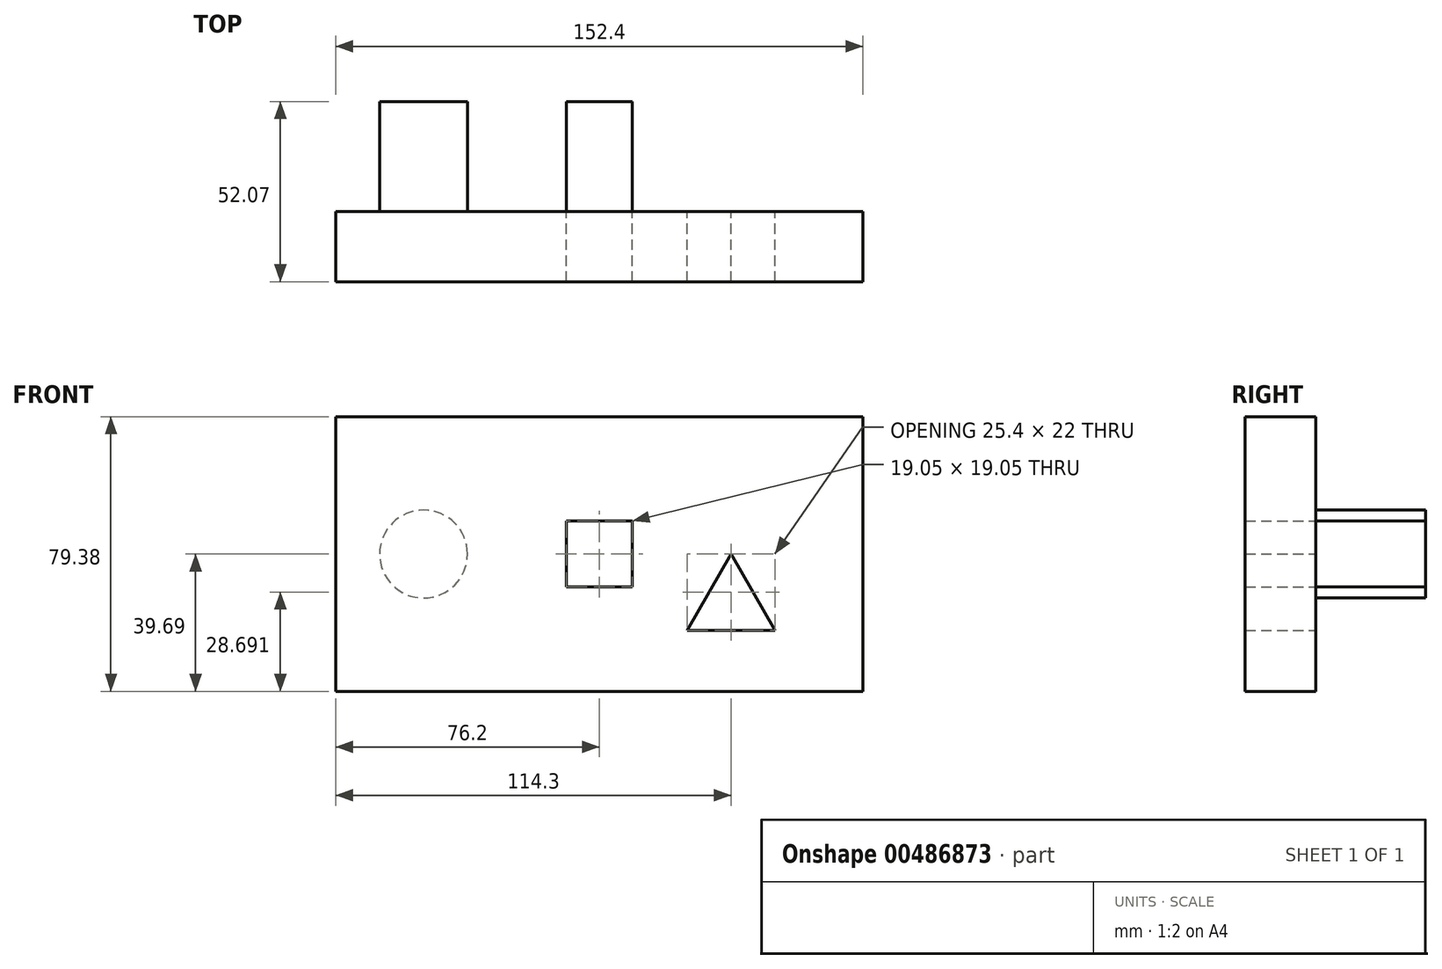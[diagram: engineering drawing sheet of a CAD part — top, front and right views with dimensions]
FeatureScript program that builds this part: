
annotation { "Feature Type Name" : "Feature", "Feature Type Description" : "" }
export const myFeature = defineFeature(function(context is Context, id is Id, definition is map)
    precondition{}
    {
        {
            var Q0;
            Q0=qCreatedBy(makeId("Front.planeOp"),FACE);
            var sketch = newSketch(context, id + "F0", { "sketchPlane" : qUnion([Q0])});
            skLineSegment(sketch, "E0", {"start": v(0, 0) * mm, "end": v(44.45, 0) * mm});
            skLineSegment(sketch, "E1", {"start": v(0, 0) * mm, "end": v(-31.75, 0) * mm});
            skLineSegment(sketch, "E2.bottom", {"start": v(-107.95, 39.69) * mm, "end": v(44.45, 39.69) * mm});
            skLineSegment(sketch, "E2.top", {"start": v(-107.95, -39.69) * mm, "end": v(44.45, -39.69) * mm});
            skLineSegment(sketch, "E2.left", {"start": v(-107.95, 39.69) * mm, "end": v(-107.95, -39.69) * mm});
            skLineSegment(sketch, "E2.right", {"start": v(44.45, 39.69) * mm, "end": v(44.45, -39.69) * mm});
            skPoint(sketch, "E2.middle", {"position": v(-31.75, 0) * mm});
            skLineSegment(sketch, "E3.bottom", {"start": v(-41.27, 9.53) * mm, "end": v(-22.22, 9.53) * mm});
            skLineSegment(sketch, "E3.top", {"start": v(-41.27, -9.53) * mm, "end": v(-22.22, -9.53) * mm});
            skLineSegment(sketch, "E3.left", {"start": v(-41.27, 9.53) * mm, "end": v(-41.27, -9.53) * mm});
            skLineSegment(sketch, "E3.right", {"start": v(-22.22, 9.53) * mm, "end": v(-22.22, -9.53) * mm});
            skLineSegment(sketch, "E4", {"start": v(-31.75, 0) * mm, "end": v(-82.55, 0) * mm});
            skCircle(sketch, "E5", {"center": v(-82.55, 0) * mm, "radius": 12.7 * mm});
            skLineSegment(sketch, "E6", {"start": v(6.35, 0) * mm, "end": v(-6.35, -22) * mm});
            skLineSegment(sketch, "E7", {"start": v(-6.35, -22) * mm, "end": v(19.05, -22) * mm});
            skLineSegment(sketch, "E8", {"start": v(19.05, -22) * mm, "end": v(6.35, 0) * mm});
            skLineSegment(sketch, "E9", {"start": v(6.35, 0) * mm, "end": v(0, 0) * mm});
            skSolve(sketch);
        }
        {
            var Q0;
            {var subQ9=sQuery(id+"F0.wireOp",EDGE,"E2.bottom");Q0=makeQuery(id+"F0.imprint","IMPRINT",FACE,{"disambiguationData":[TD([[makeQuery(id+"F0.imprint","IMPRINT",EDGE,{"derivedFrom":subQ9}),-1.0]])]});}
            var Q1;
            Q1=makeQuery(id+"F0.imprint","IMPRINT",FACE,{"disambiguationData":[TD([[makeQuery(id+"F0.imprint","IMPRINT",EDGE,{"derivedFrom":sQuery(id+"F0.wireOp",EDGE,"E5")}),1.0]])]});
            extrude(context, id + "F1", {"entities" : qUnion([Q0, Q1]), "depth" : 20.32 * mm});
        }
        {
            var Q0;
            Q0=makeQuery(id+"F0.imprint","IMPRINT",FACE,{"disambiguationData":[TD([[makeQuery(id+"F0.imprint","IMPRINT",EDGE,{"derivedFrom":sQuery(id+"F0.wireOp",EDGE,"E5")}),1.0]])]});
            var Q1;
            {var subQ1=sQuery(id+"F0.wireOp",EDGE,"E3.top");Q1=makeQuery(id+"F0.imprint","IMPRINT",FACE,{"disambiguationData":[TD([[makeQuery(id+"F0.imprint","IMPRINT",EDGE,{"derivedFrom":subQ1}),1.0]])]});}
            var Q2;
            {var subQ1=sQuery(id+"F0.wireOp",EDGE,"E3.bottom");Q2=makeQuery(id+"F0.imprint","IMPRINT",FACE,{"disambiguationData":[TD([[makeQuery(id+"F0.imprint","IMPRINT",EDGE,{"derivedFrom":subQ1}),-1.0]])]});}
            extrude(context, id + "F2", {"entities" : qUnion([Q0, Q1, Q2]), "oppositeDirection" : true, "depth" : 31.75 * mm});
        }
    });
